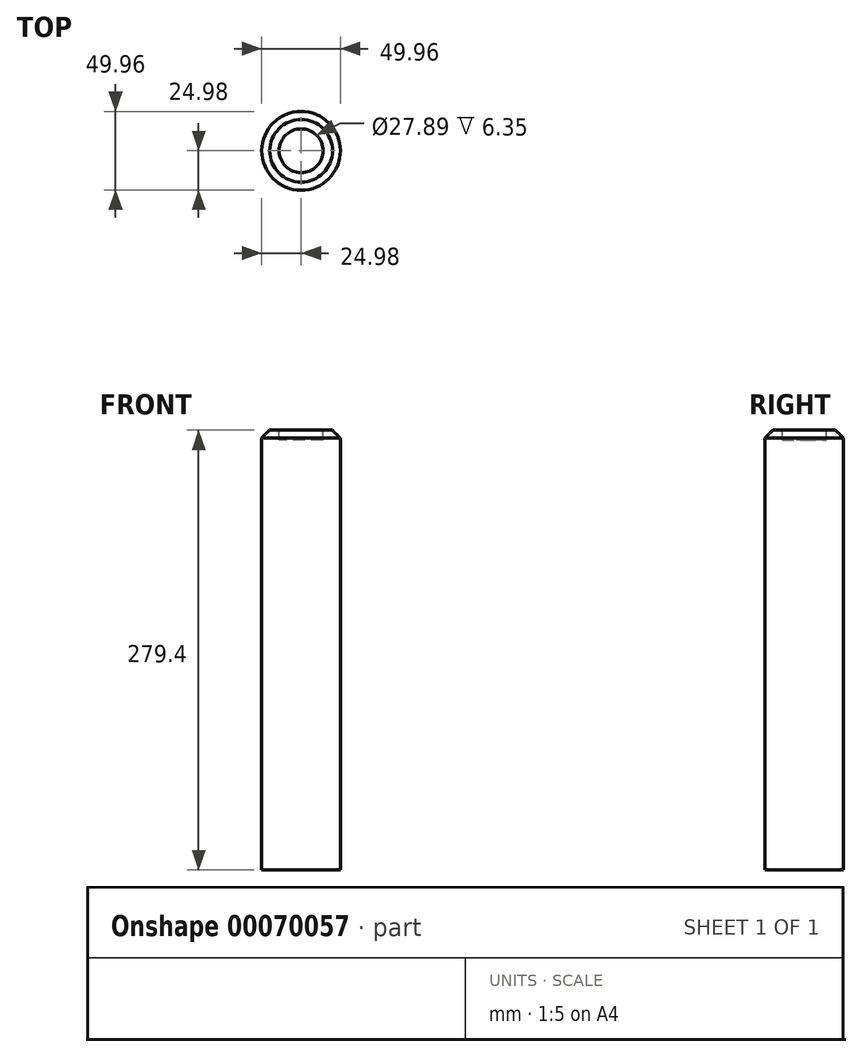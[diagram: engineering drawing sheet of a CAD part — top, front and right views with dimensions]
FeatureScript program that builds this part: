
annotation { "Feature Type Name" : "Feature", "Feature Type Description" : "" }
export const myFeature = defineFeature(function(context is Context, id is Id, definition is map)
    precondition{}
    {
        {
            var Q0;
            Q0=qCreatedBy(makeId("Top.planeOp"),FACE);
            var sketch = newSketch(context, id + "F0", { "sketchPlane" : qUnion([Q0])});
            skCircle(sketch, "E0", {"center": v(0, 0) * mm, "radius": 24.98 * mm});
            skSolve(sketch);
        }
        {
            var Q0;
            Q0=makeQuery(id+"F0.imprint","IMPRINT",FACE,{"disambiguationData":[TD([[makeQuery(id+"F0.imprint","IMPRINT",EDGE,{"derivedFrom":sQuery(id+"F0.wireOp",EDGE,"E0")}),1.0]])]});
            extrude(context, id + "F1", {"entities" : qUnion([Q0]), "depth" : 279.4 * mm});
        }
        {
            var Q0;
            Q0=makeQuery(id+"F1.opExtrude","CAP_EDGE",EDGE,{"disambiguationData":[OSD([sQuery(id+"F0.wireOp",EDGE,"E0")])],"isStart":false});
            chamfer(context, id + "F2", {"entities" : qUnion([Q0]), "width" : 5.08 * mm, "tangentPropagation" : true});
        }
        {
            var Q0;
            Q0=makeQuery(id+"F1.opExtrude","CAP_FACE",FACE,{"disambiguationData":[OSD([sQuery(id+"F0.wireOp",EDGE,"E0")])],"isStart":false});
            var sketch = newSketch(context, id + "F3", { "sketchPlane" : qUnion([Q0])});
            skCircle(sketch, "E1", {"center": v(0, 0) * mm, "radius": 13.94 * mm});
            skSolve(sketch);
        }
        {
            var Q0;
            Q0=qSketchRegion(id+"F3",true);
            extrude(context, id + "F4", {"entities" : qUnion([Q0]), "operationType" : NewBodyOperationType.REMOVE, "oppositeDirection" : true, "depth" : 6.35 * mm});
        }
    });
